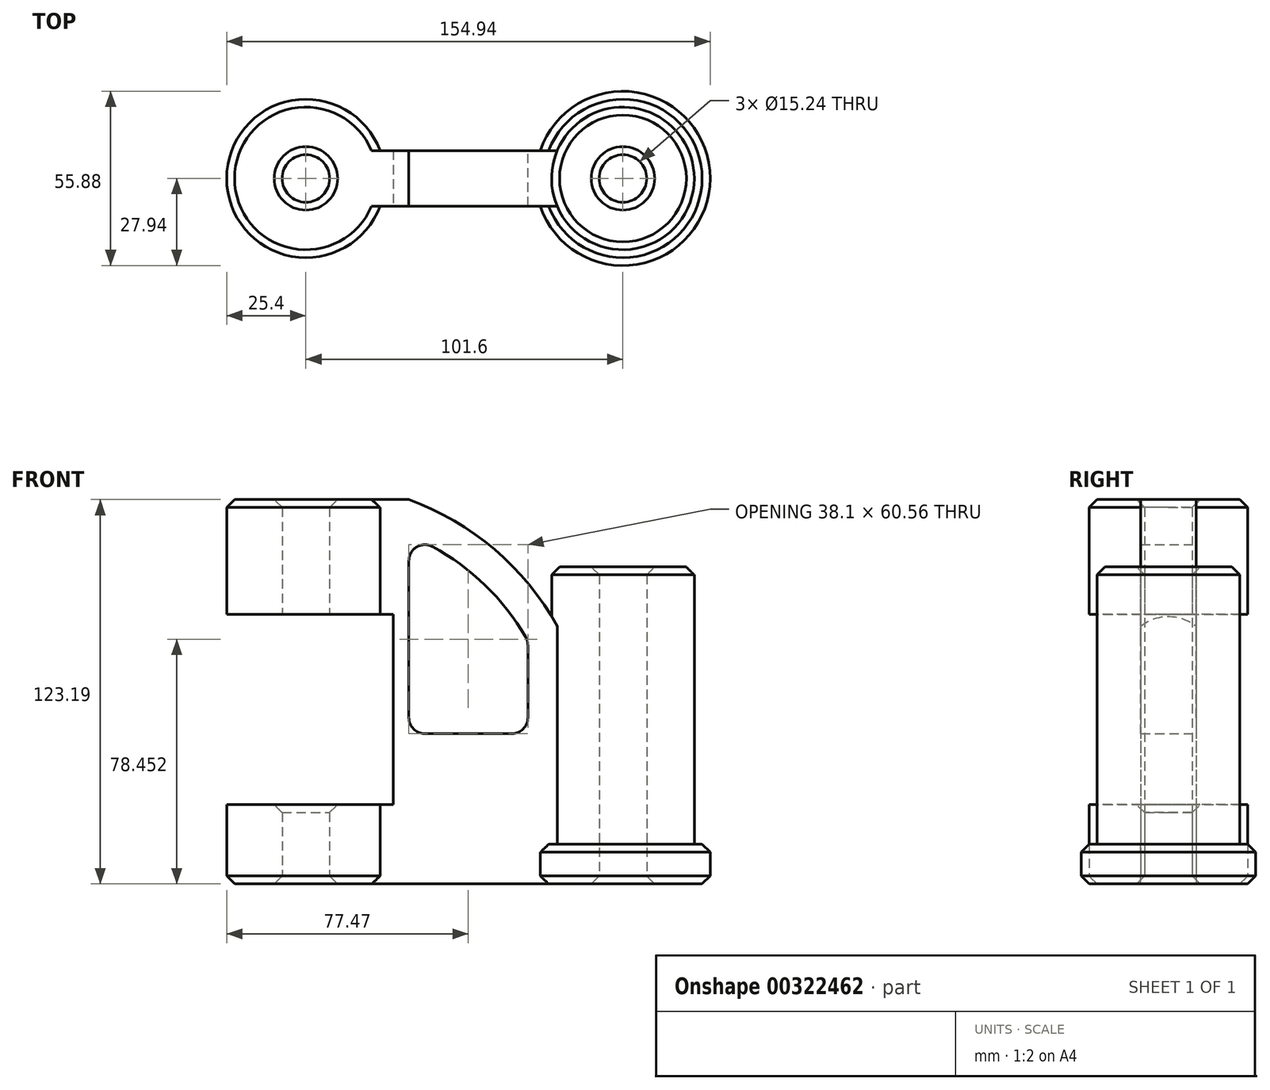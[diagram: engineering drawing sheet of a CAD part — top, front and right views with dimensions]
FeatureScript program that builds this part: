
annotation { "Feature Type Name" : "Feature", "Feature Type Description" : "" }
export const myFeature = defineFeature(function(context is Context, id is Id, definition is map)
    precondition{}
    {
        {
            var Q0;
            Q0=qCreatedBy(makeId("Top.planeOp"),FACE);
            var sketch = newSketch(context, id + "F0", { "sketchPlane" : qUnion([Q0])});
            skCircle(sketch, "E0", {"center": v(0, 0) * mm, "radius": 25.4 * mm});
            skCircle(sketch, "E1", {"center": v(0, 0) * mm, "radius": 7.62 * mm});
            skCircle(sketch, "E2", {"center": v(101.6, 0) * mm, "radius": 22.86 * mm});
            skCircle(sketch, "E3", {"center": v(101.6, 0) * mm, "radius": 7.62 * mm});
            skSolve(sketch);
        }
        {
            var Q0;
            Q0=makeQuery(id+"F0.imprint","IMPRINT",FACE,{"disambiguationData":[TD([[makeQuery(id+"F0.imprint","IMPRINT",EDGE,{"derivedFrom":sQuery(id+"F0.wireOp",EDGE,"E0")}),1.0]])]});
            var Q1;
            Q1=sQuery(id+"F0.wireOp",EDGE,"E0");
            extrude(context, id + "F1", {"entities" : qUnion([Q0]), "surfaceEntities" : qUnion([Q1]), "depth" : 123.19 * mm});
        }
        {
            var Q0;
            Q0=makeQuery(id+"F0.imprint","IMPRINT",FACE,{"disambiguationData":[TD([[makeQuery(id+"F0.imprint","IMPRINT",EDGE,{"derivedFrom":sQuery(id+"F0.wireOp",EDGE,"E2")}),1.0]])]});
            var sketch = newSketch(context, id + "F2", { "sketchPlane" : qUnion([Q0])});
            skSolve(sketch);
        }
        {
            var Q0;
            Q0 = qSketchRegion(id + "F2", true);
            var Q1;
            Q1=makeQuery(id+"F0.imprint","IMPRINT",FACE,{"disambiguationData":[TD([[makeQuery(id+"F0.imprint","IMPRINT",EDGE,{"derivedFrom":sQuery(id+"F0.wireOp",EDGE,"E2")}),1.0]])]});
            extrude(context, id + "F3", {"entities" : qUnion([Q0, Q1]), "depth" : 101.6 * mm});
        }
        {
            var Q0;
            Q0=qCreatedBy(makeId("Front.planeOp"),FACE);
            var sketch = newSketch(context, id + "F4", { "sketchPlane" : qUnion([Q0])});
            skLineSegment(sketch, "E4", {"start": v(20.32, 0) * mm, "end": v(20.32, 123.2) * mm});
            skArc(sketch, "E5", {"start": v(81.28, 81.28) * mm, "mid": v(61.05, 106.72) * mm, "end": v(33.02, 123.2) * mm});
            skLineSegment(sketch, "E6", {"start": v(81.28, 81.28) * mm, "end": v(81.28, 0) * mm});
            skLineSegment(sketch, "E7", {"start": v(81.28, 0) * mm, "end": v(20.32, 0) * mm});
            skLineSegment(sketch, "E8", {"start": v(20.32, 123.2) * mm, "end": v(33.02, 123.2) * mm});
            skArc(sketch, "E9.0", {"start": v(71.12, 77.99) * mm, "mid": v(54.92, 98.05) * mm, "end": v(33.02, 111.67) * mm});
            skLineSegment(sketch, "E10", {"start": v(33.02, 111.67) * mm, "end": v(33.02, 48.17) * mm});
            skLineSegment(sketch, "E11", {"start": v(33.02, 48.17) * mm, "end": v(71.12, 48.17) * mm});
            skLineSegment(sketch, "E12", {"start": v(71.12, 48.17) * mm, "end": v(71.12, 77.99) * mm});
            skSolve(sketch);
        }
        {
            var Q0;
            Q0=makeQuery(id+"F4.imprint","IMPRINT",FACE,{"disambiguationData":[TD([[makeQuery(id+"F4.imprint","IMPRINT",EDGE,{"derivedFrom":sQuery(id+"F4.wireOp",EDGE,"E4")}),-1.0]])]});
            extrude(context, id + "F5", {"entities" : qUnion([Q0]), "operationType" : NewBodyOperationType.ADD, "depth" : 17.78 * mm, "symmetric" : true});
        }
        {
            var Q0;
            Q0=qCreatedBy(makeId("Front.planeOp"),FACE);
            var sketch = newSketch(context, id + "F6", { "sketchPlane" : qUnion([Q0])});
            skLineSegment(sketch, "E13.bottom", {"start": v(-33.02, 86.36) * mm, "end": v(27.94, 86.36) * mm});
            skLineSegment(sketch, "E13.top", {"start": v(-33.02, 25.4) * mm, "end": v(27.94, 25.4) * mm});
            skLineSegment(sketch, "E13.left", {"start": v(-33.02, 86.36) * mm, "end": v(-33.02, 25.4) * mm});
            skLineSegment(sketch, "E13.right", {"start": v(27.94, 86.36) * mm, "end": v(27.94, 25.4) * mm});
            skSolve(sketch);
        }
        {
            var Q0;
            Q0 = qSketchRegion(id + "F6", true);
            extrude(context, id + "F7", {"entities" : qUnion([Q0]), "operationType" : NewBodyOperationType.REMOVE, "oppositeDirection" : true, "depth" : 101.6 * mm, "symmetric" : true});
        }
        {
            var Q0;
            Q0=makeQuery(id+"F5.opExtrude","SWEPT_EDGE",EDGE,{"disambiguationData":[OSD([sQuery(id+"F4.wireOp",EDGE,"E9.0"),sQuery(id+"F4.wireOp",EDGE,"E10")])]});
            var Q1;
            Q1=makeQuery(id+"F5.opExtrude","SWEPT_EDGE",EDGE,{"disambiguationData":[OSD([sQuery(id+"F4.wireOp",EDGE,"E9.0"),sQuery(id+"F4.wireOp",EDGE,"E12")])]});
            var Q2;
            Q2=makeQuery(id+"F5.opExtrude","SWEPT_EDGE",EDGE,{"disambiguationData":[OSD([sQuery(id+"F4.wireOp",EDGE,"E10"),sQuery(id+"F4.wireOp",EDGE,"E11")])]});
            var Q3;
            Q3=makeQuery(id+"F5.opExtrude","SWEPT_EDGE",EDGE,{"disambiguationData":[OSD([sQuery(id+"F4.wireOp",EDGE,"E11"),sQuery(id+"F4.wireOp",EDGE,"E12")])]});
            fillet(context, id + "F8", {"entities" : qUnion([Q0, Q1, Q2, Q3]), "radius" : 5.08 * mm, "tangentPropagation" : true, "allowEdgeOverflow" : false});
        }
        {
            var Q0;
            Q0=makeQuery(id+"F1.opExtrude","CAP_EDGE",EDGE,{"disambiguationData":[OSD([sQuery(id+"F0.wireOp",EDGE,"E1")])],"isStart":false});
            var Q1;
            Q1=makeQuery(id+"F1.opExtrude","CAP_EDGE",EDGE,{"disambiguationData":[OSD([sQuery(id+"F0.wireOp",EDGE,"E0")])],"isStart":false});
            var Q2;
            Q2=makeQuery(id+"F7.boolean.opBoolean","INTERSECT",EDGE,{"derivedFrom":[makeQuery(id+"F1.opExtrude","SWEPT_FACE",FACE,{"disambiguationData":[OSD([sQuery(id+"F0.wireOp",EDGE,"E1")])]}),makeQuery(id+"F7.opExtrude","SWEPT_FACE",FACE,{"disambiguationData":[OSD([sQuery(id+"F6.wireOp",EDGE,"E13.top")])]})]});
            var Q3;
            Q3=makeQuery(id+"F1.opExtrude","CAP_EDGE",EDGE,{"disambiguationData":[OSD([sQuery(id+"F0.wireOp",EDGE,"E1")])],"isStart":true});
            var Q4;
            Q4=makeQuery(id+"F1.opExtrude","CAP_EDGE",EDGE,{"disambiguationData":[OSD([sQuery(id+"F0.wireOp",EDGE,"E0")])],"isStart":true});
            chamfer(context, id + "F9", {"entities" : qUnion([Q0, Q1, Q2, Q3, Q4]), "width" : 2.54 * mm, "tangentPropagation" : true});
        }
        {
            var Q0;
            Q0=qCreatedBy(makeId("Top.planeOp"),FACE);
            var sketch = newSketch(context, id + "F10", { "sketchPlane" : qUnion([Q0])});
            skCircle(sketch, "E14.0", {"center": v(101.6, 0) * mm, "radius": 22.86 * mm});
            skCircle(sketch, "E15.0", {"center": v(101.6, 0) * mm, "radius": 27.94 * mm});
            skSolve(sketch);
        }
        {
            var Q0;
            Q0=makeQuery(id+"F10.imprint","IMPRINT",FACE,{"disambiguationData":[TD([[makeQuery(id+"F10.imprint","IMPRINT",EDGE,{"derivedFrom":sQuery(id+"F10.wireOp",EDGE,"E14.0")}),-1.0]])]});
            extrude(context, id + "F11", {"entities" : qUnion([Q0]), "operationType" : NewBodyOperationType.ADD, "depth" : 12.7 * mm});
        }
        {
            var Q0;
            Q0=makeQuery(id+"F3.opExtrude","CAP_EDGE",EDGE,{"disambiguationData":[OSD([sQuery(id+"F0.wireOp",EDGE,"E3")])],"isStart":true});
            var Q1;
            Q1=makeQuery(id+"F11.opExtrude","CAP_EDGE",EDGE,{"disambiguationData":[OSD([sQuery(id+"F10.wireOp",EDGE,"E15.0")])],"isStart":true});
            var Q2;
            Q2=makeQuery(id+"F3.opExtrude","CAP_EDGE",EDGE,{"disambiguationData":[OSD([sQuery(id+"F0.wireOp",EDGE,"E3")])],"isStart":false});
            var Q3;
            Q3=makeQuery(id+"F11.opExtrude","CAP_EDGE",EDGE,{"disambiguationData":[OSD([sQuery(id+"F10.wireOp",EDGE,"E15.0")])],"isStart":false});
            var Q4;
            Q4=makeQuery(id+"F3.opExtrude","CAP_EDGE",EDGE,{"disambiguationData":[OSD([sQuery(id+"F0.wireOp",EDGE,"E2")])],"isStart":false});
            chamfer(context, id + "F12", {"entities" : qUnion([Q0, Q1, Q2, Q3, Q4]), "width" : 2.54 * mm, "tangentPropagation" : true});
        }
    });
